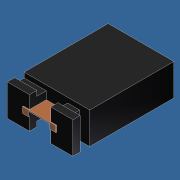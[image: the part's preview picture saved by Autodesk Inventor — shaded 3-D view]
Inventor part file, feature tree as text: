
AUTODESK INVENTOR PART (.ipt)
format: ipt  version: 2012 (Build 160160000, 160)  size: 150,528 bytes
history: native  units: in
note: dims shown in document units (in); Inventor stores cm internally (conversion verified against a paired STEP export)
features: extrude x5, sketch x5, projected_geometry x3
ambient origin geometry x8: Origin, YZ Plane, XZ Plane, XY Plane, X Axis, Y Axis, Z Axis, Center Point
bodies: Solid1 (feature_tree)
feature tree (13):
  extrude  "Extrusion1"  Depth=0.094in
  extrude  "Extrusion2"  Depth=0.066in
  extrude  "Extrusion3"  Depth=0.05in
  extrude  "Extrusion4"  Depth=0.022in
  extrude  "Extrusion5"  Depth=0.03in
  sketch  "Sketch1"  dims[d0=0.195in d1=0.094in]
  sketch  "Sketch2"  dims[d2=0.3in d3=0.0in d4=0.066in]
  sketch  "Sketch3"  dims[d5=0.066in d6=0.05in]
  sketch  "Sketch4"  dims[d7=0.531in d8=0.0in d9=0.022in]
  projected_geometry  "Projected Loop1"
  sketch  "Sketch5"  dims[d12=0.0in d13=0.03in d14=0.03in d15=0.015in d16=0.015in d17=0.531in d18=0.0in d19=0.018in d20=0.018in d21=0.018in d22=0.018in d23=0.038in d24=0.038in d25=0.038in d26=0.005in d27=0.0in d28=0.0525in d29=0.0in]
  projected_geometry  "Projected Loop2"
  projected_geometry  "Projected Loop3"
